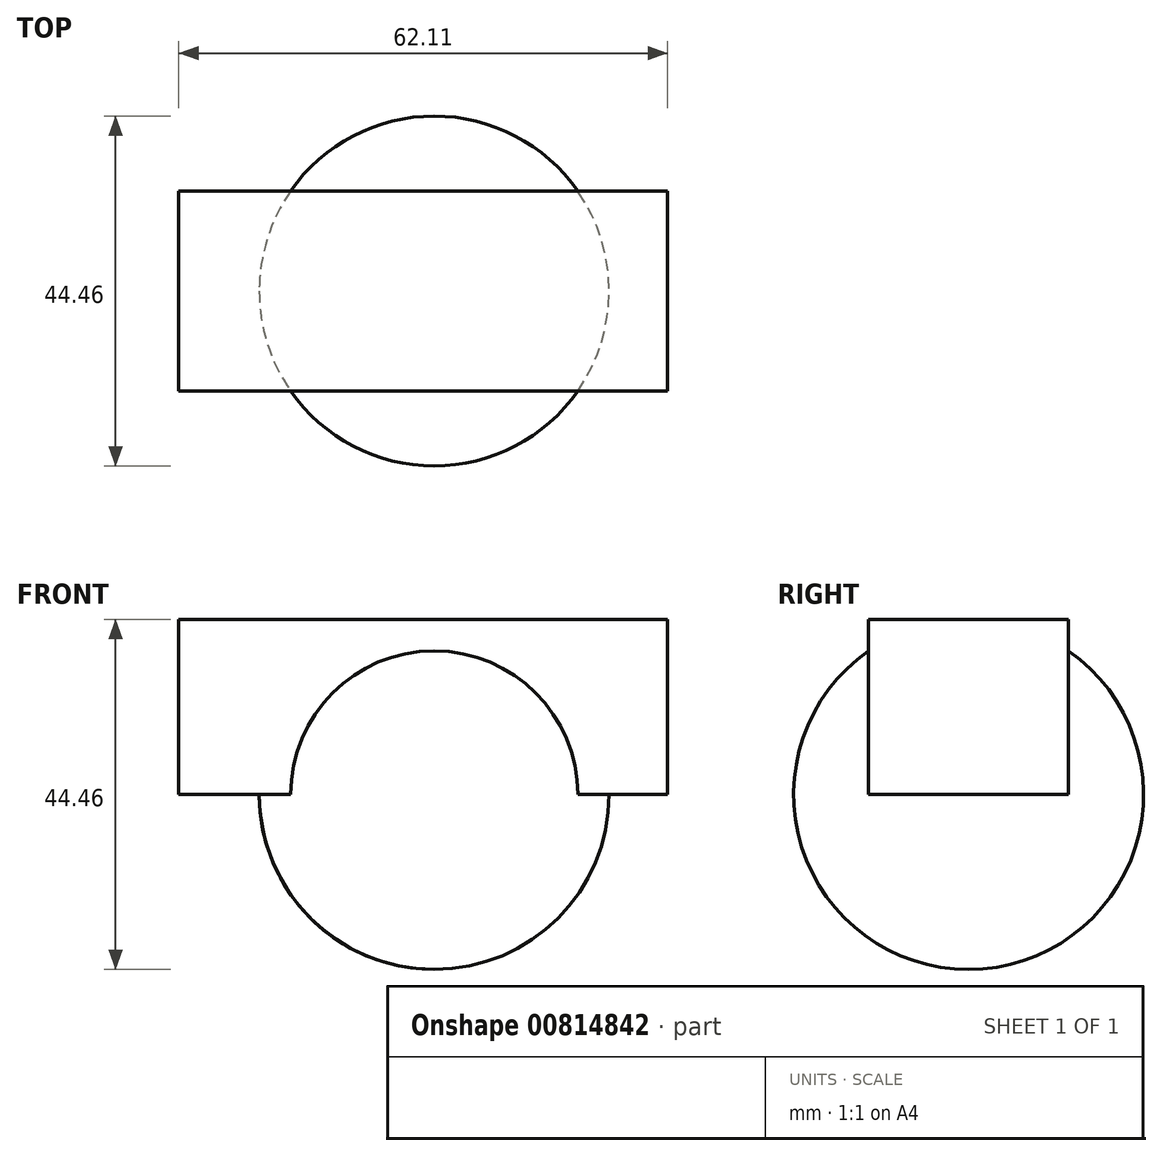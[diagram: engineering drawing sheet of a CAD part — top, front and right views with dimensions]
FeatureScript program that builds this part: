
annotation { "Feature Type Name" : "Feature", "Feature Type Description" : "" }
export const myFeature = defineFeature(function(context is Context, id is Id, definition is map)
    precondition{}
    {
        {
            var Q0;
            Q0=qCreatedBy(makeId("Front.planeOp"),FACE);
            var sketch = newSketch(context, id + "F0", { "sketchPlane" : qUnion([Q0])});
            skArc(sketch, "E0", {"start": v(0, -22.23) * mm, "mid": v(22.23, 0) * mm, "end": v(0, 22.23) * mm});
            skLineSegment(sketch, "E1", {"start": v(0, 22.23) * mm, "end": v(0, -22.23) * mm});
            skSolve(sketch);
        }
        {
            var Q0;
            Q0=makeQuery(id+"F0.imprint","IMPRINT",FACE,{"disambiguationData":[TD([[makeQuery(id+"F0.imprint","IMPRINT",EDGE,{"derivedFrom":sQuery(id+"F0.wireOp",EDGE,"E0")}),1.0]])]});
            var Q1;
            Q1=sQuery(id+"F0.wireOp",EDGE,"E1");
            revolve(context, id + "F1", {"surfaceOperationType" : NewSurfaceOperationType.NEW, "entities" : qUnion([Q0]), "axis" : qUnion([Q1]), "revolveType" : RevolveType.FULL});
        }
        {
            var Q0;
            Q0=qCreatedBy(makeId("Front.planeOp"),FACE);
            var sketch = newSketch(context, id + "F2", { "sketchPlane" : qUnion([Q0])});
            skLineSegment(sketch, "E2.bottom", {"start": v(29.65, 0) * mm, "end": v(-32.46, 0) * mm});
            skLineSegment(sketch, "E2.top", {"start": v(29.65, 22.23) * mm, "end": v(-32.46, 22.22) * mm});
            skLineSegment(sketch, "E2.left", {"start": v(29.65, 0) * mm, "end": v(29.65, 22.23) * mm});
            skLineSegment(sketch, "E2.right", {"start": v(-32.46, 0) * mm, "end": v(-32.46, 22.22) * mm});
            skSolve(sketch);
        }
        {
            var Q0;
            Q0=makeQuery(id+"F2.imprint","IMPRINT",FACE,{"disambiguationData":[TD([[makeQuery(id+"F2.imprint","IMPRINT",EDGE,{"derivedFrom":sQuery(id+"F2.wireOp",EDGE,"E2.bottom")}),-1.0]])]});
            extrude(context, id + "F3", {"entities" : qUnion([Q0]), "operationType" : NewBodyOperationType.ADD, "endBound" : BoundingType.SYMMETRIC, "depth" : 25.4 * mm, "offsetDistance" : 25.4 * mm});
        }
    });
